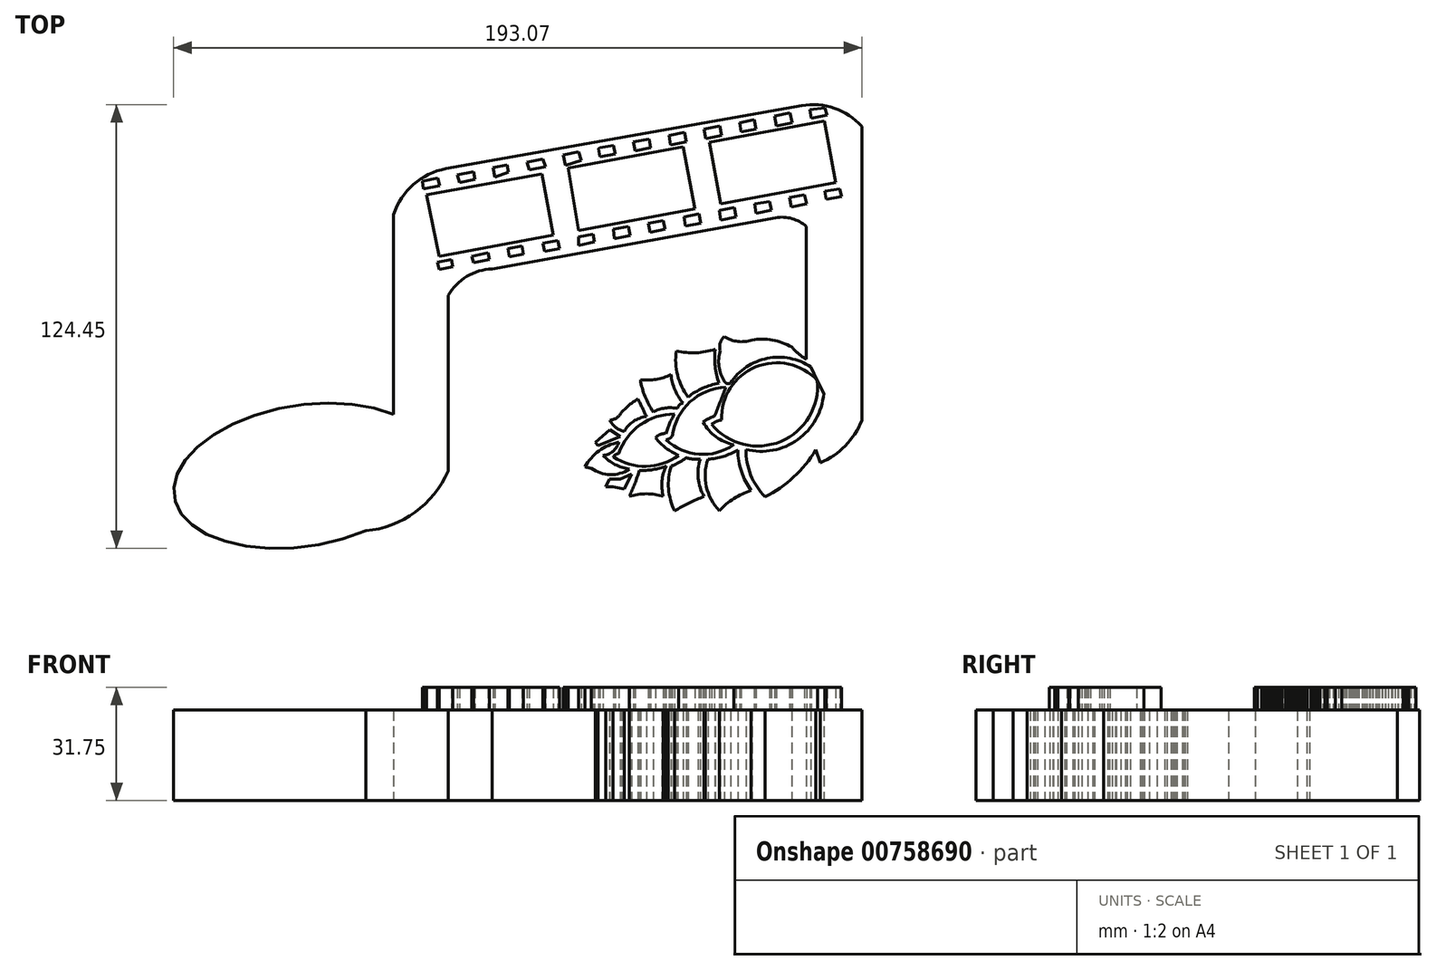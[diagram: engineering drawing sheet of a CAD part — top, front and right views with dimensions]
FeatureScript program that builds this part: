
annotation { "Feature Type Name" : "Feature", "Feature Type Description" : "" }
export const myFeature = defineFeature(function(context is Context, id is Id, definition is map)
    precondition{}
    {
        {
            var Q0;
            Q0=qCreatedBy(makeId("Top.planeOp"),FACE);
            var sketch = newSketch(context, id + "F0", { "sketchPlane" : qUnion([Q0])});
            skEllipse(sketch, "E0", {"center": v(-77.2, -44.65) * mm, "majorRadius": 36.69 * mm, "minorRadius": 19.76 * mm, "majorAxis": v(0.99, 0.16)});
            skArc(sketch, "E1", {"start": v(-59.67, -60.12) * mm, "mid": v(-45.83, -54.9) * mm, "end": v(-36.56, -43.36) * mm});
            skLineSegment(sketch, "E2", {"start": v(-36.56, -43.36) * mm, "end": v(-36.56, 5.92) * mm});
            skLineSegment(sketch, "E3", {"start": v(-51.85, -27.46) * mm, "end": v(-51.85, 28.63) * mm});
            skArc(sketch, "E4", {"start": v(-37.13, 41.47) * mm, "mid": v(-46.28, 37.1) * mm, "end": v(-51.85, 28.63) * mm});
            skArc(sketch, "E5", {"start": v(-24.2, 13.39) * mm, "mid": v(-31.34, 11.24) * mm, "end": v(-36.56, 5.92) * mm});
            skLineSegment(sketch, "E6", {"start": v(-37.13, 41.47) * mm, "end": v(62.67, 59.15) * mm});
            skLineSegment(sketch, "E7", {"start": v(-24.2, 13.39) * mm, "end": v(55.34, 27.72) * mm});
            skArc(sketch, "E8", {"start": v(79.52, 53.33) * mm, "mid": v(71.85, 58.43) * mm, "end": v(62.67, 59.15) * mm});
            skLineSegment(sketch, "E9", {"start": v(79.52, 53.33) * mm, "end": v(79.52, -29.17) * mm});
            skArc(sketch, "E10", {"start": v(63.99, 25.25) * mm, "mid": v(59.95, 27.49) * mm, "end": v(55.34, 27.72) * mm});
            skLineSegment(sketch, "E11", {"start": v(63.99, 25.25) * mm, "end": v(63.99, -12) * mm});
            skArc(sketch, "E12", {"start": v(67.9, -41) * mm, "mid": v(74.9, -36.27) * mm, "end": v(79.52, -29.17) * mm});
            skLineSegment(sketch, "E13", {"start": v(67.9, -41) * mm, "end": v(66.59, -37.4) * mm});
            skArc(sketch, "E14", {"start": v(59.87, -8.55) * mm, "mid": v(61.79, -10.44) * mm, "end": v(63.99, -12) * mm});
            skArc(sketch, "E15", {"start": v(59.87, -8.55) * mm, "mid": v(54.45, -6.58) * mm, "end": v(48.7, -6.57) * mm});
            skArc(sketch, "E16", {"start": v(40.96, -5.6) * mm, "mid": v(44.71, -7) * mm, "end": v(48.7, -6.57) * mm});
            skArc(sketch, "E17", {"start": v(40.96, -5.6) * mm, "mid": v(39.81, -7.42) * mm, "end": v(39.78, -9.57) * mm});
            skArc(sketch, "E18", {"start": v(39.78, -9.57) * mm, "mid": v(39.44, -14) * mm, "end": v(40.96, -18.17) * mm});
            skArc(sketch, "E19", {"start": v(40.96, -18.17) * mm, "mid": v(41.71, -18.79) * mm, "end": v(42.68, -18.65) * mm});
            skArc(sketch, "E20", {"start": v(65.24, -14.14) * mm, "mid": v(53.02, -11.7) * mm, "end": v(42.68, -18.65) * mm});
            skArc(sketch, "E21", {"start": v(65.24, -14.14) * mm, "mid": v(65.03, -12.82) * mm, "end": v(63.99, -12) * mm});
            skArc(sketch, "E22", {"start": v(66.59, -37.4) * mm, "mid": v(69.93, -29.84) * mm, "end": v(68.83, -21.65) * mm});
            skLineSegment(sketch, "E23", {"start": v(68.83, -21.65) * mm, "end": v(65.24, -14.14) * mm});
            skArc(sketch, "E24", {"start": v(47.02, -37.29) * mm, "mid": v(61.55, -34.53) * mm, "end": v(68.83, -21.65) * mm});
            skArc(sketch, "E25", {"start": v(47.02, -37.29) * mm, "mid": v(48.38, -44.45) * mm, "end": v(52.35, -50.57) * mm});
            skArc(sketch, "E26", {"start": v(52.35, -50.57) * mm, "mid": v(60.43, -45.03) * mm, "end": v(66.59, -37.4) * mm});
            skArc(sketch, "E27", {"start": v(27.5, -9.67) * mm, "mid": v(32.99, -10.15) * mm, "end": v(38.4, -9.14) * mm});
            skArc(sketch, "E28", {"start": v(27.5, -9.67) * mm, "mid": v(27.83, -16.45) * mm, "end": v(30.77, -22.56) * mm});
            skArc(sketch, "E29", {"start": v(39.47, -18.7) * mm, "mid": v(34.9, -20.1) * mm, "end": v(30.77, -22.56) * mm});
            skArc(sketch, "E30", {"start": v(38.4, -9.14) * mm, "mid": v(38.36, -13.98) * mm, "end": v(39.47, -18.7) * mm});
            skArc(sketch, "E31", {"start": v(17.4, -17.73) * mm, "mid": v(21.8, -17.62) * mm, "end": v(26, -16.28) * mm});
            skArc(sketch, "E32", {"start": v(17.4, -17.73) * mm, "mid": v(18.7, -22.44) * mm, "end": v(21, -26.75) * mm});
            skArc(sketch, "E33", {"start": v(27.87, -25.79) * mm, "mid": v(24.35, -25.66) * mm, "end": v(21, -26.75) * mm});
            skArc(sketch, "E34", {"start": v(29.38, -24.28) * mm, "mid": v(28.37, -24.78) * mm, "end": v(27.87, -25.79) * mm});
            skArc(sketch, "E35", {"start": v(26, -16.28) * mm, "mid": v(27.09, -20.53) * mm, "end": v(29.38, -24.28) * mm});
            skArc(sketch, "E36", {"start": v(16.7, -23.1) * mm, "mid": v(14.32, -24.78) * mm, "end": v(12.19, -26.75) * mm});
            skArc(sketch, "E37", {"start": v(8.8, -29.06) * mm, "mid": v(10.82, -28.38) * mm, "end": v(12.19, -26.75) * mm});
            skArc(sketch, "E38", {"start": v(8.8, -29.06) * mm, "mid": v(10.47, -31.08) * mm, "end": v(12.83, -32.23) * mm});
            skArc(sketch, "E39", {"start": v(19.06, -28.04) * mm, "mid": v(15.46, -29.4) * mm, "end": v(12.83, -32.23) * mm});
            skArc(sketch, "E40", {"start": v(19.06, -28.04) * mm, "mid": v(17.91, -25.56) * mm, "end": v(16.7, -23.1) * mm});
            skLineSegment(sketch, "E41", {"start": v(11.76, -33.63) * mm, "end": v(8.8, -31.75) * mm});
            skLineSegment(sketch, "E42", {"start": v(8.8, -31.75) * mm, "end": v(4.72, -35.3) * mm});
            skLineSegment(sketch, "E43", {"start": v(4.72, -35.3) * mm, "end": v(5.56, -36.26) * mm});
            skLineSegment(sketch, "E44", {"start": v(5.56, -36.26) * mm, "end": v(11.76, -33.63) * mm});
            skLineSegment(sketch, "E45", {"start": v(14.87, -44.21) * mm, "end": v(12.89, -48.35) * mm});
            skLineSegment(sketch, "E46", {"start": v(12.89, -48.35) * mm, "end": v(9.72, -47.7) * mm});
            skLineSegment(sketch, "E47", {"start": v(9.72, -47.7) * mm, "end": v(7.68, -47.7) * mm});
            skLineSegment(sketch, "E48", {"start": v(7.68, -47.7) * mm, "end": v(8.75, -45.6) * mm});
            skLineSegment(sketch, "E49", {"start": v(8.75, -45.6) * mm, "end": v(11.76, -45.6) * mm});
            skLineSegment(sketch, "E50", {"start": v(11.76, -45.6) * mm, "end": v(14.87, -44.21) * mm});
            skArc(sketch, "E51", {"start": v(17.13, -43.24) * mm, "mid": v(20.94, -42.92) * mm, "end": v(24.65, -41.95) * mm});
            skArc(sketch, "E52", {"start": v(24.65, -41.95) * mm, "mid": v(23.47, -46.12) * mm, "end": v(23.84, -50.44) * mm});
            skArc(sketch, "E53", {"start": v(23.84, -50.44) * mm, "mid": v(19.09, -49.73) * mm, "end": v(14.34, -50.44) * mm});
            skArc(sketch, "E54", {"start": v(14.34, -50.44) * mm, "mid": v(15.83, -46.88) * mm, "end": v(17.13, -43.24) * mm});
            skArc(sketch, "E55", {"start": v(26.05, -41.95) * mm, "mid": v(28.23, -40.93) * mm, "end": v(30.24, -39.6) * mm});
            skArc(sketch, "E56", {"start": v(30.24, -39.6) * mm, "mid": v(32.2, -39.98) * mm, "end": v(34.21, -40.02) * mm});
            skArc(sketch, "E57", {"start": v(34.21, -40.02) * mm, "mid": v(33.62, -45.35) * mm, "end": v(35.28, -50.44) * mm});
            skArc(sketch, "E58", {"start": v(35.28, -50.44) * mm, "mid": v(31.06, -52.3) * mm, "end": v(27.01, -54.52) * mm});
            skArc(sketch, "E59", {"start": v(26.05, -41.95) * mm, "mid": v(25.3, -48.33) * mm, "end": v(27.01, -54.52) * mm});
            skArc(sketch, "E60", {"start": v(36.36, -40.02) * mm, "mid": v(40.7, -39.23) * mm, "end": v(44.74, -37.44) * mm});
            skArc(sketch, "E61", {"start": v(36.36, -40.02) * mm, "mid": v(35.9, -47.73) * mm, "end": v(39.58, -54.52) * mm});
            skArc(sketch, "E62", {"start": v(48.5, -48.83) * mm, "mid": v(43.64, -51.05) * mm, "end": v(39.58, -54.52) * mm});
            skArc(sketch, "E63", {"start": v(44.74, -37.44) * mm, "mid": v(45.75, -43.42) * mm, "end": v(48.5, -48.83) * mm});
            skLineSegment(sketch, "E64", {"start": v(-51.85, -27.46) * mm, "end": v(-51.85, -27.51) * mm});
            skLineSegment(sketch, "E65", {"start": v(-59.67, -60.12) * mm, "end": v(-59.94, -60.15) * mm});
            skSolve(sketch);
        }
        {
            var Q0;
            Q0 = qSketchRegion(id + "F0", true);
            extrude(context, id + "F1", {"entities" : qUnion([Q0]), "depth" : 25.4 * mm, "offsetDistance" : 25.4 * mm});
        }
        {
            var Q0;
            Q0=makeQuery(id+"F1.opExtrude","CAP_FACE",FACE,{"disambiguationData":[OSD([sQuery(id+"F0.wireOp",EDGE,"E0"),sQuery(id+"F0.wireOp",EDGE,"E1"),sQuery(id+"F0.wireOp",EDGE,"E2"),sQuery(id+"F0.wireOp",EDGE,"E3"),sQuery(id+"F0.wireOp",EDGE,"E4"),sQuery(id+"F0.wireOp",EDGE,"E5"),sQuery(id+"F0.wireOp",EDGE,"E6"),sQuery(id+"F0.wireOp",EDGE,"E7"),sQuery(id+"F0.wireOp",EDGE,"E8"),sQuery(id+"F0.wireOp",EDGE,"E9"),sQuery(id+"F0.wireOp",EDGE,"E10"),sQuery(id+"F0.wireOp",EDGE,"E11"),sQuery(id+"F0.wireOp",EDGE,"E12"),sQuery(id+"F0.wireOp",EDGE,"E13"),sQuery(id+"F0.wireOp",EDGE,"E14"),sQuery(id+"F0.wireOp",EDGE,"E15"),sQuery(id+"F0.wireOp",EDGE,"E16"),sQuery(id+"F0.wireOp",EDGE,"E17"),sQuery(id+"F0.wireOp",EDGE,"E18"),sQuery(id+"F0.wireOp",EDGE,"E19"),sQuery(id+"F0.wireOp",EDGE,"E20"),sQuery(id+"F0.wireOp",EDGE,"E23"),sQuery(id+"F0.wireOp",EDGE,"E24"),sQuery(id+"F0.wireOp",EDGE,"E25"),sQuery(id+"F0.wireOp",EDGE,"E26")])],"isStart":false});
            var sketch = newSketch(context, id + "F2", { "sketchPlane" : qUnion([Q0])});
            skLineSegment(sketch, "E66", {"start": v(-39.12, 16.93) * mm, "end": v(-42.6, 34.17) * mm});
            skLineSegment(sketch, "E67", {"start": v(-42.6, 34.17) * mm, "end": v(-10.2, 40.05) * mm});
            skLineSegment(sketch, "E68", {"start": v(-10.2, 40.05) * mm, "end": v(-7.1, 22.9) * mm});
            skLineSegment(sketch, "E69", {"start": v(-7.1, 22.9) * mm, "end": v(-39.12, 16.93) * mm});
            skLineSegment(sketch, "E70", {"start": v(-2.83, 41.62) * mm, "end": v(29.4, 47.63) * mm});
            skLineSegment(sketch, "E71", {"start": v(29.4, 47.63) * mm, "end": v(32.65, 30.21) * mm});
            skLineSegment(sketch, "E72", {"start": v(32.65, 30.21) * mm, "end": v(0, 24.13) * mm});
            skLineSegment(sketch, "E73", {"start": v(0, 24.13) * mm, "end": v(-2.83, 41.62) * mm});
            skLineSegment(sketch, "E74", {"start": v(36.77, 48.91) * mm, "end": v(68.97, 54.91) * mm});
            skLineSegment(sketch, "E75", {"start": v(68.97, 54.91) * mm, "end": v(72.2, 37.64) * mm});
            skLineSegment(sketch, "E76", {"start": v(72.2, 37.64) * mm, "end": v(39.94, 31.63) * mm});
            skLineSegment(sketch, "E77", {"start": v(39.94, 31.63) * mm, "end": v(36.77, 48.91) * mm});
            skLineSegment(sketch, "E78", {"start": v(-43.52, 35.83) * mm, "end": v(-38.98, 36.7) * mm});
            skLineSegment(sketch, "E79", {"start": v(-38.98, 36.7) * mm, "end": v(-39.39, 38.84) * mm});
            skLineSegment(sketch, "E80", {"start": v(-39.39, 38.84) * mm, "end": v(-43.79, 38) * mm});
            skLineSegment(sketch, "E81", {"start": v(-43.79, 38) * mm, "end": v(-43.52, 35.83) * mm});
            skLineSegment(sketch, "E82", {"start": v(-35.64, 16.02) * mm, "end": v(-35.23, 13.97) * mm});
            skLineSegment(sketch, "E83", {"start": v(-35.23, 13.97) * mm, "end": v(-39.12, 13.19) * mm});
            skLineSegment(sketch, "E84", {"start": v(-39.12, 13.19) * mm, "end": v(-39.53, 15.25) * mm});
            skLineSegment(sketch, "E85", {"start": v(-39.53, 15.25) * mm, "end": v(-35.64, 16.02) * mm});
            skLineSegment(sketch, "E86", {"start": v(-33.38, 37.64) * mm, "end": v(-29, 38.43) * mm});
            skLineSegment(sketch, "E87", {"start": v(-29, 38.43) * mm, "end": v(-29.46, 40.65) * mm});
            skLineSegment(sketch, "E88", {"start": v(-29.46, 40.65) * mm, "end": v(-33.93, 39.74) * mm});
            skLineSegment(sketch, "E89", {"start": v(-33.93, 39.74) * mm, "end": v(-33.38, 37.64) * mm});
            skLineSegment(sketch, "E90", {"start": v(-29.9, 16.93) * mm, "end": v(-25.29, 17.87) * mm});
            skLineSegment(sketch, "E91", {"start": v(-25.29, 17.87) * mm, "end": v(-24.91, 16.02) * mm});
            skLineSegment(sketch, "E92", {"start": v(-24.91, 16.02) * mm, "end": v(-29.46, 15.1) * mm});
            skLineSegment(sketch, "E93", {"start": v(-29.46, 15.1) * mm, "end": v(-29.9, 16.93) * mm});
            skLineSegment(sketch, "E94", {"start": v(-23.97, 41.77) * mm, "end": v(-19.98, 42.5) * mm});
            skLineSegment(sketch, "E95", {"start": v(-19.98, 42.5) * mm, "end": v(-19.57, 40.45) * mm});
            skLineSegment(sketch, "E96", {"start": v(-19.57, 40.45) * mm, "end": v(-23.44, 39.1) * mm});
            skLineSegment(sketch, "E97", {"start": v(-23.44, 39.1) * mm, "end": v(-23.97, 41.77) * mm});
            skLineSegment(sketch, "E98", {"start": v(-19.7, 19.1) * mm, "end": v(-15.84, 19.81) * mm});
            skLineSegment(sketch, "E99", {"start": v(-15.84, 19.81) * mm, "end": v(-15.39, 17.55) * mm});
            skLineSegment(sketch, "E100", {"start": v(-15.39, 17.55) * mm, "end": v(-19.4, 16.74) * mm});
            skLineSegment(sketch, "E101", {"start": v(-19.4, 16.74) * mm, "end": v(-19.7, 19.1) * mm});
            skLineSegment(sketch, "E102", {"start": v(-9.96, 20.56) * mm, "end": v(-5.73, 21.35) * mm});
            skLineSegment(sketch, "E103", {"start": v(-5.73, 21.35) * mm, "end": v(-5.28, 19.1) * mm});
            skLineSegment(sketch, "E104", {"start": v(-5.28, 19.1) * mm, "end": v(-9.52, 18.23) * mm});
            skLineSegment(sketch, "E105", {"start": v(-9.52, 18.23) * mm, "end": v(-9.96, 20.56) * mm});
            skLineSegment(sketch, "E106", {"start": v(-13.83, 41.1) * mm, "end": v(-9.23, 42.03) * mm});
            skLineSegment(sketch, "E107", {"start": v(-9.23, 42.03) * mm, "end": v(-9.96, 44.24) * mm});
            skLineSegment(sketch, "E108", {"start": v(-9.96, 44.24) * mm, "end": v(-14.36, 43.35) * mm});
            skLineSegment(sketch, "E109", {"start": v(-14.36, 43.35) * mm, "end": v(-13.83, 41.1) * mm});
            skLineSegment(sketch, "E110", {"start": v(-4.23, 45.37) * mm, "end": v(0, 46.23) * mm});
            skLineSegment(sketch, "E111", {"start": v(0, 46.23) * mm, "end": v(0.8, 43.84) * mm});
            skLineSegment(sketch, "E112", {"start": v(0.8, 43.84) * mm, "end": v(-3.59, 42.39) * mm});
            skLineSegment(sketch, "E113", {"start": v(-3.59, 42.39) * mm, "end": v(-4.23, 45.37) * mm});
            skLineSegment(sketch, "E114", {"start": v(0, 22.3) * mm, "end": v(4.1, 23.12) * mm});
            skLineSegment(sketch, "E115", {"start": v(4.1, 23.12) * mm, "end": v(4.55, 20.91) * mm});
            skLineSegment(sketch, "E116", {"start": v(4.55, 20.91) * mm, "end": v(0, 20) * mm});
            skLineSegment(sketch, "E117", {"start": v(0, 20) * mm, "end": v(0, 22.3) * mm});
            skLineSegment(sketch, "E118", {"start": v(9.83, 24.45) * mm, "end": v(14.05, 25.3) * mm});
            skLineSegment(sketch, "E119", {"start": v(14.05, 25.3) * mm, "end": v(14.55, 22.79) * mm});
            skLineSegment(sketch, "E120", {"start": v(14.55, 22.79) * mm, "end": v(10.1, 21.89) * mm});
            skLineSegment(sketch, "E121", {"start": v(10.1, 21.89) * mm, "end": v(9.83, 24.45) * mm});
            skLineSegment(sketch, "E122", {"start": v(5.6, 47.13) * mm, "end": v(6.07, 47.36) * mm});
            skLineSegment(sketch, "E123", {"start": v(6.07, 47.36) * mm, "end": v(9.83, 47.97) * mm});
            skLineSegment(sketch, "E124", {"start": v(9.83, 47.97) * mm, "end": v(10.3, 45.64) * mm});
            skLineSegment(sketch, "E125", {"start": v(10.3, 45.64) * mm, "end": v(6.07, 44.79) * mm});
            skLineSegment(sketch, "E126", {"start": v(6.07, 44.79) * mm, "end": v(5.6, 47.13) * mm});
            skLineSegment(sketch, "E127", {"start": v(15.49, 49.07) * mm, "end": v(19.9, 49.79) * mm});
            skLineSegment(sketch, "E128", {"start": v(19.9, 49.79) * mm, "end": v(20.3, 47.36) * mm});
            skLineSegment(sketch, "E129", {"start": v(20.3, 47.36) * mm, "end": v(15.89, 46.47) * mm});
            skLineSegment(sketch, "E130", {"start": v(15.89, 46.47) * mm, "end": v(15.49, 49.07) * mm});
            skLineSegment(sketch, "E131", {"start": v(25.42, 50.77) * mm, "end": v(29.74, 51.64) * mm});
            skLineSegment(sketch, "E132", {"start": v(29.74, 51.64) * mm, "end": v(30.26, 49.07) * mm});
            skLineSegment(sketch, "E133", {"start": v(30.26, 49.07) * mm, "end": v(25.81, 48.18) * mm});
            skLineSegment(sketch, "E134", {"start": v(25.81, 48.18) * mm, "end": v(25.42, 50.77) * mm});
            skLineSegment(sketch, "E135", {"start": v(35.27, 52.62) * mm, "end": v(39.63, 53.41) * mm});
            skLineSegment(sketch, "E136", {"start": v(39.63, 53.41) * mm, "end": v(40.16, 50.77) * mm});
            skLineSegment(sketch, "E137", {"start": v(40.16, 50.77) * mm, "end": v(35.79, 49.95) * mm});
            skLineSegment(sketch, "E138", {"start": v(35.79, 49.95) * mm, "end": v(35.27, 52.62) * mm});
            skLineSegment(sketch, "E139", {"start": v(45.25, 54.36) * mm, "end": v(49.36, 55.19) * mm});
            skLineSegment(sketch, "E140", {"start": v(49.36, 55.19) * mm, "end": v(49.88, 52.62) * mm});
            skLineSegment(sketch, "E141", {"start": v(49.88, 52.62) * mm, "end": v(45.7, 51.84) * mm});
            skLineSegment(sketch, "E142", {"start": v(45.7, 51.84) * mm, "end": v(45.25, 54.36) * mm});
            skLineSegment(sketch, "E143", {"start": v(55.08, 56.26) * mm, "end": v(59.42, 57.13) * mm});
            skLineSegment(sketch, "E144", {"start": v(59.42, 57.13) * mm, "end": v(59.98, 54.36) * mm});
            skLineSegment(sketch, "E145", {"start": v(59.98, 54.36) * mm, "end": v(55.58, 53.47) * mm});
            skLineSegment(sketch, "E146", {"start": v(55.58, 53.47) * mm, "end": v(55.08, 56.26) * mm});
            skLineSegment(sketch, "E147", {"start": v(65, 58.02) * mm, "end": v(69.1, 58.51) * mm});
            skLineSegment(sketch, "E148", {"start": v(69.1, 58.51) * mm, "end": v(69.78, 56.48) * mm});
            skLineSegment(sketch, "E149", {"start": v(69.78, 56.48) * mm, "end": v(65.4, 55.6) * mm});
            skLineSegment(sketch, "E150", {"start": v(65.4, 55.6) * mm, "end": v(65, 58.02) * mm});
            skLineSegment(sketch, "E151", {"start": v(19.65, 26.21) * mm, "end": v(23.8, 26.89) * mm});
            skLineSegment(sketch, "E152", {"start": v(23.8, 26.89) * mm, "end": v(24.3, 24.45) * mm});
            skLineSegment(sketch, "E153", {"start": v(24.3, 24.45) * mm, "end": v(20.12, 23.6) * mm});
            skLineSegment(sketch, "E154", {"start": v(20.12, 23.6) * mm, "end": v(19.65, 26.21) * mm});
            skLineSegment(sketch, "E155", {"start": v(29.62, 27.94) * mm, "end": v(33.88, 28.8) * mm});
            skLineSegment(sketch, "E156", {"start": v(33.88, 28.8) * mm, "end": v(34.4, 26.21) * mm});
            skLineSegment(sketch, "E157", {"start": v(34.4, 26.21) * mm, "end": v(30.05, 25.34) * mm});
            skLineSegment(sketch, "E158", {"start": v(30.05, 25.34) * mm, "end": v(29.62, 27.94) * mm});
            skLineSegment(sketch, "E159", {"start": v(39.53, 29.7) * mm, "end": v(39.9, 29.85) * mm});
            skLineSegment(sketch, "E160", {"start": v(39.9, 29.85) * mm, "end": v(43.74, 30.62) * mm});
            skLineSegment(sketch, "E161", {"start": v(43.74, 30.62) * mm, "end": v(44.28, 27.94) * mm});
            skLineSegment(sketch, "E162", {"start": v(44.28, 27.94) * mm, "end": v(39.9, 27.06) * mm});
            skLineSegment(sketch, "E163", {"start": v(39.9, 27.06) * mm, "end": v(39.53, 29.7) * mm});
            skLineSegment(sketch, "E164", {"start": v(49.48, 31.6) * mm, "end": v(53.7, 32.28) * mm});
            skLineSegment(sketch, "E165", {"start": v(53.7, 32.28) * mm, "end": v(54.18, 29.85) * mm});
            skLineSegment(sketch, "E166", {"start": v(54.18, 29.85) * mm, "end": v(49.84, 28.97) * mm});
            skLineSegment(sketch, "E167", {"start": v(49.84, 28.97) * mm, "end": v(49.48, 31.6) * mm});
            skLineSegment(sketch, "E168", {"start": v(59.26, 33.34) * mm, "end": v(63.5, 34.13) * mm});
            skLineSegment(sketch, "E169", {"start": v(63.5, 34.13) * mm, "end": v(64, 31.6) * mm});
            skLineSegment(sketch, "E170", {"start": v(64, 31.6) * mm, "end": v(59.79, 30.75) * mm});
            skLineSegment(sketch, "E171", {"start": v(59.79, 30.75) * mm, "end": v(59.26, 33.34) * mm});
            skLineSegment(sketch, "E172", {"start": v(69.12, 35.18) * mm, "end": v(73.38, 35.87) * mm});
            skLineSegment(sketch, "E173", {"start": v(73.38, 35.87) * mm, "end": v(73.84, 33.62) * mm});
            skLineSegment(sketch, "E174", {"start": v(73.84, 33.62) * mm, "end": v(69.54, 32.92) * mm});
            skLineSegment(sketch, "E175", {"start": v(69.54, 32.92) * mm, "end": v(69.12, 35.18) * mm});
            skArc(sketch, "E176", {"start": v(67.03, -17.9) * mm, "mid": v(49.74, -14.15) * mm, "end": v(40.16, -29.02) * mm});
            skArc(sketch, "E177", {"start": v(40.16, -29.02) * mm, "mid": v(38.72, -29.47) * mm, "end": v(37.42, -30.25) * mm});
            skArc(sketch, "E178", {"start": v(37.42, -30.25) * mm, "mid": v(56.8, -35.03) * mm, "end": v(67.03, -17.9) * mm});
            skArc(sketch, "E179", {"start": v(38.22, -28) * mm, "mid": v(39.82, -23.93) * mm, "end": v(41.34, -19.83) * mm});
            skArc(sketch, "E180", {"start": v(38.22, -28) * mm, "mid": v(36.53, -28.65) * mm, "end": v(35, -29.6) * mm});
            skArc(sketch, "E181", {"start": v(35, -29.6) * mm, "mid": v(38.6, -33.71) * mm, "end": v(43.6, -35.95) * mm});
            skArc(sketch, "E182", {"start": v(24.63, -34.55) * mm, "mid": v(33.86, -38.63) * mm, "end": v(43.6, -35.95) * mm});
            skArc(sketch, "E183", {"start": v(24.63, -34.55) * mm, "mid": v(25.6, -34.19) * mm, "end": v(26.35, -33.48) * mm});
            skArc(sketch, "E184", {"start": v(41.34, -19.83) * mm, "mid": v(31.36, -23.92) * mm, "end": v(26.35, -33.48) * mm});
            skArc(sketch, "E185", {"start": v(27, -27.35) * mm, "mid": v(25.6, -30) * mm, "end": v(24.63, -32.83) * mm});
            skArc(sketch, "E186", {"start": v(24.63, -32.83) * mm, "mid": v(23, -33.05) * mm, "end": v(21.68, -34.01) * mm});
            skArc(sketch, "E187", {"start": v(21.68, -34.01) * mm, "mid": v(24.58, -36.9) * mm, "end": v(28.12, -38.96) * mm});
            skArc(sketch, "E188", {"start": v(9.8, -39.39) * mm, "mid": v(19.03, -42) * mm, "end": v(28.12, -38.96) * mm});
            skArc(sketch, "E189", {"start": v(11.31, -38.42) * mm, "mid": v(10.45, -38.74) * mm, "end": v(9.8, -39.39) * mm});
            skArc(sketch, "E190", {"start": v(27, -27.35) * mm, "mid": v(17.36, -30.35) * mm, "end": v(11.31, -38.42) * mm});
            skArc(sketch, "E191", {"start": v(11.31, -35.24) * mm, "mid": v(5.8, -37.68) * mm, "end": v(1.8, -42.18) * mm});
            skArc(sketch, "E192", {"start": v(3.63, -42.55) * mm, "mid": v(8.9, -44.34) * mm, "end": v(14.26, -42.82) * mm});
            skArc(sketch, "E193", {"start": v(6.9, -38.96) * mm, "mid": v(9.7, -37.8) * mm, "end": v(11.31, -35.24) * mm});
            skArc(sketch, "E194", {"start": v(6.9, -38.96) * mm, "mid": v(10.28, -41.47) * mm, "end": v(14.26, -42.82) * mm});
            skArc(sketch, "E195", {"start": v(1.8, -42.18) * mm, "mid": v(2.71, -42.38) * mm, "end": v(3.63, -42.55) * mm});
            skSolve(sketch);
        }
        {
            var Q0;
            Q0 = qSketchRegion(id + "F2", true);
            extrude(context, id + "F3", {"entities" : qUnion([Q0]), "operationType" : NewBodyOperationType.ADD, "depth" : 6.35 * mm, "offsetDistance" : 25.4 * mm});
        }
    });
